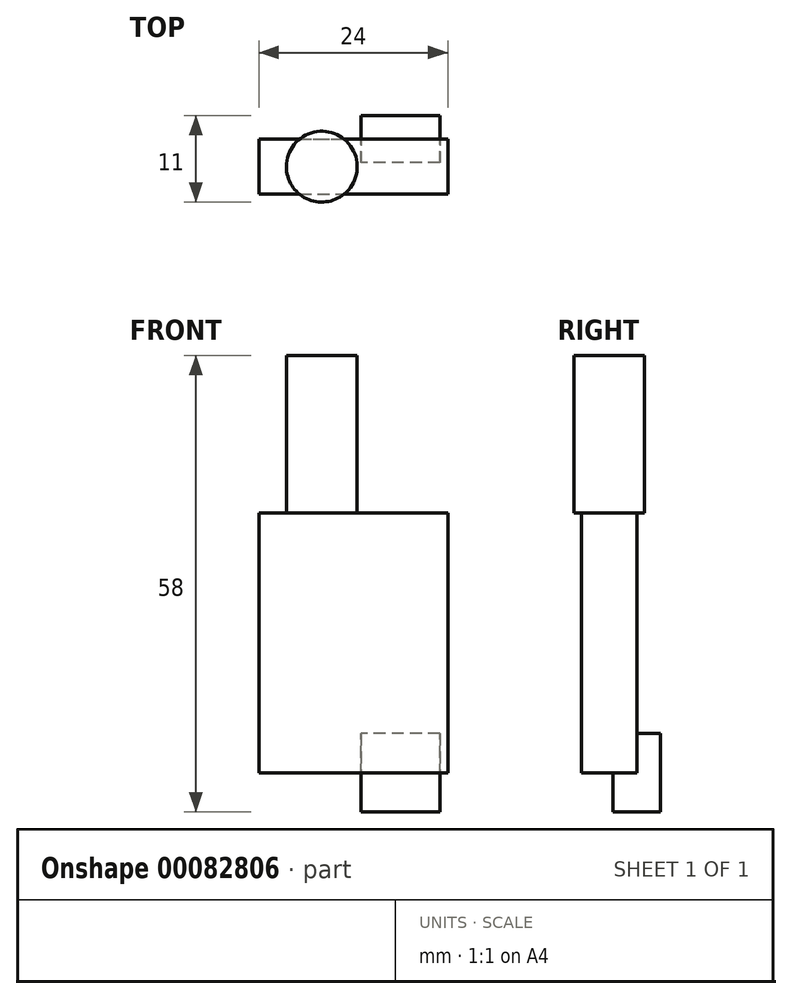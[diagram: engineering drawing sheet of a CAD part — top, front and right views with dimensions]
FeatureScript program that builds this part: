
annotation { "Feature Type Name" : "Feature", "Feature Type Description" : "" }
export const myFeature = defineFeature(function(context is Context, id is Id, definition is map)
    precondition{}
    {
        {
            var Q0;
            Q0=qCreatedBy(makeId("Front.planeOp"),FACE);
            var sketch = newSketch(context, id + "F0", { "sketchPlane" : qUnion([Q0])});
            skLineSegment(sketch, "E0.bottom", {"start": v(12, 16.5) * mm, "end": v(-12, 16.5) * mm});
            skLineSegment(sketch, "E0.top", {"start": v(12, -16.5) * mm, "end": v(-12, -16.5) * mm});
            skLineSegment(sketch, "E0.left", {"start": v(12, 16.5) * mm, "end": v(12, -16.5) * mm});
            skLineSegment(sketch, "E0.right", {"start": v(-12, 16.5) * mm, "end": v(-12, -16.5) * mm});
            skPoint(sketch, "E0.middle", {"position": v(0, 0) * mm});
            skLineSegment(sketch, "E1.bottom", {"start": v(-1, -21.5) * mm, "end": v(-11, -21.5) * mm});
            skLineSegment(sketch, "E1.top", {"start": v(-1, -11.5) * mm, "end": v(-11, -11.5) * mm});
            skLineSegment(sketch, "E1.left", {"start": v(-1, -21.5) * mm, "end": v(-1, -11.5) * mm});
            skLineSegment(sketch, "E1.right", {"start": v(-11, -21.5) * mm, "end": v(-11, -11.5) * mm});
            skPoint(sketch, "E1.middle", {"position": v(-6, -16.5) * mm});
            skSolve(sketch);
        }
        {
            var Q0;
            Q0=makeQuery(id+"F0.imprint","IMPRINT",FACE,{"disambiguationData":[TD([[makeQuery(id+"F0.imprint","IMPRINT",EDGE,{"derivedFrom":sQuery(id+"F0.wireOp",EDGE,"E0.bottom")}),1.0]])]});
            var Q1;
            {var subQ5=sQuery(id+"F0.wireOp",EDGE,"E1.top");Q1=makeQuery(id+"F0.imprint","IMPRINT",FACE,{"disambiguationData":[TD([[makeQuery(id+"F0.imprint","IMPRINT",EDGE,{"derivedFrom":subQ5}),1.0]])]});}
            extrude(context, id + "F1", {"entities" : qUnion([Q0, Q1]), "oppositeDirection" : true, "depth" : 7 * mm});
        }
        {
            var Q0;
            {var subQ5=sQuery(id+"F0.wireOp",EDGE,"E1.bottom");Q0=makeQuery(id+"F0.imprint","IMPRINT",FACE,{"disambiguationData":[TD([[makeQuery(id+"F0.imprint","IMPRINT",EDGE,{"derivedFrom":subQ5}),-1.0]])]});}
            var Q1;
            {var subQ5=sQuery(id+"F0.wireOp",EDGE,"E1.top");Q1=makeQuery(id+"F0.imprint","IMPRINT",FACE,{"disambiguationData":[TD([[makeQuery(id+"F0.imprint","IMPRINT",EDGE,{"derivedFrom":subQ5}),1.0]])]});}
            extrude(context, id + "F2", {"entities" : qUnion([Q0, Q1]), "operationType" : NewBodyOperationType.ADD, "endBound" : BoundingType.SYMMETRIC, "depth" : 6 * mm});
        }
        {
            var Q0;
            Q0=makeQuery(id+"F1.opExtrude","SWEPT_FACE",FACE,{"disambiguationData":[OSD([sQuery(id+"F0.wireOp",EDGE,"E0.bottom")])]});
            var sketch = newSketch(context, id + "F3", { "sketchPlane" : qUnion([Q0])});
            skCircle(sketch, "E2", {"center": v(4, 3.5) * mm, "radius": 4.5 * mm});
            skPoint(sketch, "E2.centerSnap0", {"position": v(12, 3.5) * mm});
            skSolve(sketch);
        }
        {
            var Q0;
            Q0 = qSketchRegion(id + "F3", true);
            extrude(context, id + "F4", {"entities" : qUnion([Q0]), "operationType" : NewBodyOperationType.ADD, "depth" : 20 * mm});
        }
        {
            var Q0;
            Q0=makeQuery(id+"F1.opExtrude","SWEPT_BODY",BODY,{"disambiguationData":[OSD([sQuery(id+"F0.wireOp",EDGE,"E0.bottom"),sQuery(id+"F0.wireOp",EDGE,"E0.top"),sQuery(id+"F0.wireOp",EDGE,"E0.left"),sQuery(id+"F0.wireOp",EDGE,"E0.right")])]});
            var Q1;
            Q1=makeQuery(id+"F4.opExtrude","SWEPT_FACE",FACE,{"disambiguationData":[OSD([sQuery(id+"F3.wireOp",EDGE,"E2")])]});
            transform(context, id + "F5", {"entities" : qUnion([Q0]), "transformType" : TransformType.ROTATION, "transformAxis" : qUnion([Q1]), "angle" : 180 * degree, "makeCopy" : false});
        }
    });
